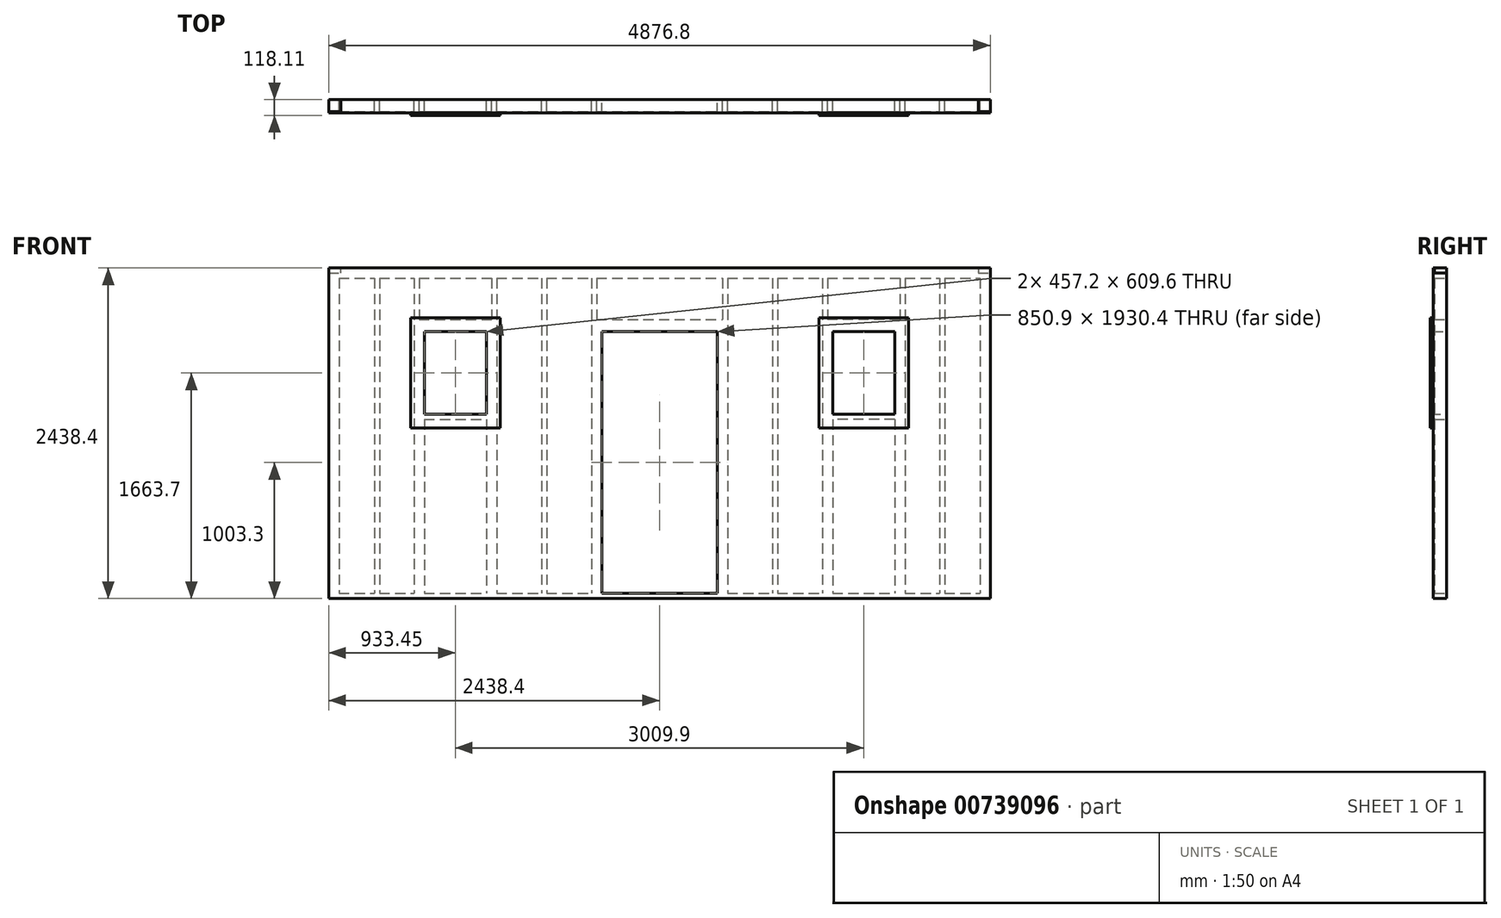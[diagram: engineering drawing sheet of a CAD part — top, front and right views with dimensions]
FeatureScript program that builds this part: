
annotation { "Feature Type Name" : "Feature", "Feature Type Description" : "" }
export const myFeature = defineFeature(function(context is Context, id is Id, definition is map)
    precondition{}
    {
        {
            var Q0;
            Q0=qCreatedBy(makeId("Front.planeOp"),FACE);
            var sketch = newSketch(context, id + "F0", { "sketchPlane" : qUnion([Q0]), "disableImprinting" : false});
            skLineSegment(sketch, "E0.bottom", {"start": v(0, 0) * mm, "end": v(4876.8, 0) * mm});
            skLineSegment(sketch, "E0.top", {"start": v(0, 2400.3) * mm, "end": v(4876.8, 2400.3) * mm});
            skLineSegment(sketch, "E0.left", {"start": v(0, 0) * mm, "end": v(0, 2400.3) * mm});
            skLineSegment(sketch, "E0.right", {"start": v(4876.8, 0) * mm, "end": v(4876.8, 2400.3) * mm});
            skLineSegment(sketch, "E1.0", {"start": v(0, 38.1) * mm, "end": v(4876.8, 38.1) * mm});
            skLineSegment(sketch, "E2.0", {"start": v(0, 2362.2) * mm, "end": v(4876.8, 2362.2) * mm});
            skLineSegment(sketch, "E3", {"start": v(38.1, 2362.2) * mm, "end": v(38.1, 38.1) * mm});
            skLineSegment(sketch, "E4.0", {"start": v(76.2, 2362.2) * mm, "end": v(76.2, 38.1) * mm});
            skLineSegment(sketch, "E5", {"start": v(4838.7, 2362.2) * mm, "end": v(4838.7, 38.1) * mm});
            skLineSegment(sketch, "E6.0", {"start": v(4800.6, 2362.2) * mm, "end": v(4800.6, 38.1) * mm});
            skLineSegment(sketch, "E7", {"start": v(336.55, 2362.2) * mm, "end": v(336.55, 38.1) * mm});
            skLineSegment(sketch, "E8.0", {"start": v(374.65, 2362.2) * mm, "end": v(374.65, 38.1) * mm});
            skLineSegment(sketch, "E9", {"start": v(628.65, 2362.2) * mm, "end": v(628.65, 38.1) * mm});
            skLineSegment(sketch, "E10.0", {"start": v(666.75, 2362.2) * mm, "end": v(666.75, 38.1) * mm});
            skLineSegment(sketch, "E11", {"start": v(1200.15, 2362.2) * mm, "end": v(1200.15, 38.1) * mm});
            skLineSegment(sketch, "E12.0", {"start": v(1238.25, 2362.2) * mm, "end": v(1238.25, 38.1) * mm});
            skLineSegment(sketch, "E13", {"start": v(666.75, 1968.5) * mm, "end": v(1200.15, 1968.5) * mm});
            skLineSegment(sketch, "E14.0", {"start": v(666.75, 2057.4) * mm, "end": v(1200.15, 2057.4) * mm});
            skLineSegment(sketch, "E15", {"start": v(666.75, 1358.9) * mm, "end": v(1200.15, 1358.9) * mm});
            skLineSegment(sketch, "E16.0", {"start": v(666.75, 1320.8) * mm, "end": v(1200.15, 1320.8) * mm});
            skLineSegment(sketch, "E17", {"start": v(704.85, 1968.5) * mm, "end": v(704.85, 1358.9) * mm});
            skLineSegment(sketch, "E18", {"start": v(1162.05, 1968.5) * mm, "end": v(1162.05, 1358.9) * mm});
            skLineSegment(sketch, "E19", {"start": v(2438.4, 2362.2) * mm, "end": v(2438.4, -1355.37) * mm, "construction": true});
            skLineSegment(sketch, "E20", {"start": v(88.9, 2400.3) * mm, "end": v(88.9, 2438.4) * mm});
            skLineSegment(sketch, "E21", {"start": v(88.9, 2438.4) * mm, "end": v(4787.9, 2438.4) * mm});
            skLineSegment(sketch, "E22", {"start": v(4787.9, 2438.4) * mm, "end": v(4787.9, 2400.3) * mm});
            skLineSegment(sketch, "E23", {"start": v(1568.45, 2362.2) * mm, "end": v(1568.45, 38.1) * mm});
            skLineSegment(sketch, "E24", {"start": v(1606.55, 2362.2) * mm, "end": v(1606.55, 38.1) * mm});
            skLineSegment(sketch, "E25.MirrorCS", {"start": v(4210.05, 1320.8) * mm, "end": v(3676.65, 1320.8) * mm});
            skLineSegment(sketch, "E26.MirrorCS", {"start": v(4540.25, 2362.2) * mm, "end": v(4540.25, 38.1) * mm});
            skLineSegment(sketch, "E27.MirrorCS", {"start": v(4502.15, 2362.2) * mm, "end": v(4502.15, 38.1) * mm});
            skLineSegment(sketch, "E28.MirrorCS", {"start": v(4248.15, 2362.2) * mm, "end": v(4248.15, 38.1) * mm});
            skLineSegment(sketch, "E29.MirrorCS", {"start": v(3270.25, 2362.2) * mm, "end": v(3270.25, 38.1) * mm});
            skLineSegment(sketch, "E30.MirrorCS", {"start": v(4171.95, 1968.5) * mm, "end": v(4171.95, 1358.9) * mm});
            skLineSegment(sketch, "E31.MirrorCS", {"start": v(4210.05, 1968.5) * mm, "end": v(3676.65, 1968.5) * mm});
            skLineSegment(sketch, "E32.MirrorCS", {"start": v(3714.75, 1968.5) * mm, "end": v(3714.75, 1358.9) * mm});
            skLineSegment(sketch, "E33.MirrorCS", {"start": v(4210.05, 1358.9) * mm, "end": v(3676.65, 1358.9) * mm});
            skLineSegment(sketch, "E34.MirrorCS", {"start": v(3308.35, 2362.2) * mm, "end": v(3308.35, 38.1) * mm});
            skLineSegment(sketch, "E35.MirrorCS", {"start": v(4210.05, 2057.4) * mm, "end": v(3676.65, 2057.4) * mm});
            skLineSegment(sketch, "E36.MirrorCS", {"start": v(4210.05, 2362.2) * mm, "end": v(4210.05, 38.1) * mm});
            skLineSegment(sketch, "E37.MirrorCS", {"start": v(3638.55, 2362.2) * mm, "end": v(3638.55, 38.1) * mm});
            skLineSegment(sketch, "E38.MirrorCS", {"start": v(3676.65, 2362.2) * mm, "end": v(3676.65, 38.1) * mm});
            skLineSegment(sketch, "E39", {"start": v(1219.2, 2813.17) * mm, "end": v(1219.2, -1320.33) * mm, "construction": true});
            skLineSegment(sketch, "E40", {"start": v(1936.75, 2362.2) * mm, "end": v(1936.75, 38.1) * mm});
            skLineSegment(sketch, "E41", {"start": v(1974.85, 2362.2) * mm, "end": v(1974.85, 38.1) * mm});
            skLineSegment(sketch, "E42.MirrorCS", {"start": v(2901.95, 2362.2) * mm, "end": v(2901.95, 38.1) * mm});
            skLineSegment(sketch, "E43.MirrorCS", {"start": v(2940.05, 2362.2) * mm, "end": v(2940.05, 38.1) * mm});
            skLineSegment(sketch, "E44", {"start": v(704.85, 1320.8) * mm, "end": v(704.85, 38.1) * mm});
            skLineSegment(sketch, "E45", {"start": v(1162.05, 1320.8) * mm, "end": v(1162.05, 38.1) * mm});
            skLineSegment(sketch, "E46", {"start": v(895.35, 2362.2) * mm, "end": v(895.35, 2057.4) * mm});
            skLineSegment(sketch, "E47", {"start": v(933.45, 2362.2) * mm, "end": v(933.45, 2057.4) * mm});
            skLineSegment(sketch, "E48", {"start": v(1974.85, 2057.4) * mm, "end": v(2901.95, 2057.4) * mm});
            skLineSegment(sketch, "E49", {"start": v(1974.85, 1968.5) * mm, "end": v(2901.95, 1968.5) * mm});
            skLineSegment(sketch, "E50", {"start": v(2012.95, 1968.5) * mm, "end": v(2012.95, 38.1) * mm});
            skLineSegment(sketch, "E51.MirrorCS", {"start": v(2863.85, 1968.5) * mm, "end": v(2863.85, 38.1) * mm});
            skLineSegment(sketch, "E52", {"start": v(3714.75, 1320.8) * mm, "end": v(3714.75, 38.1) * mm});
            skLineSegment(sketch, "E53", {"start": v(4171.95, 1320.8) * mm, "end": v(4171.95, 38.1) * mm});
            skSolve(sketch);
        }
        {
            var Q0;
            {var subQ5=sQuery(id+"F0.wireOp",EDGE,"E3");Q0=makeQuery(id+"F0.imprint","IMPRINT",FACE,{"disambiguationData":[TD([[makeQuery(id+"F0.imprint","IMPRINT",EDGE,{"derivedFrom":subQ5}),-1.0]])]});}
            var Q1;
            {var subQ0=sQuery(id+"F0.wireOp",EDGE,"E3");Q1=makeQuery(id+"F0.imprint","IMPRINT",FACE,{"disambiguationData":[TD([[makeQuery(id+"F0.imprint","IMPRINT",EDGE,{"derivedFrom":subQ0}),1.0]])]});}
            var Q2;
            {var subQ15=sQuery(id+"F0.wireOp",EDGE,"E0.bottom");Q2=makeQuery(id+"F0.imprint","IMPRINT",FACE,{"disambiguationData":[TD([[makeQuery(id+"F0.imprint","IMPRINT",EDGE,{"derivedFrom":subQ15}),1.0]])]});}
            var Q3;
            {var subQ0=sQuery(id+"F0.wireOp",EDGE,"E7");Q3=makeQuery(id+"F0.imprint","IMPRINT",FACE,{"disambiguationData":[TD([[makeQuery(id+"F0.imprint","IMPRINT",EDGE,{"derivedFrom":subQ0}),1.0]])]});}
            var Q4;
            {var subQ4=sQuery(id+"F0.wireOp",EDGE,"E9");Q4=makeQuery(id+"F0.imprint","IMPRINT",FACE,{"disambiguationData":[TD([[makeQuery(id+"F0.imprint","IMPRINT",EDGE,{"derivedFrom":subQ4}),1.0]])]});}
            var Q5;
            {var subQ5=sQuery(id+"F0.wireOp",EDGE,"E12.0");Q5=makeQuery(id+"F0.imprint","IMPRINT",FACE,{"disambiguationData":[TD([[makeQuery(id+"F0.imprint","IMPRINT",EDGE,{"derivedFrom":subQ5}),-1.0]])]});}
            var Q6;
            {var subQ5=sQuery(id+"F0.wireOp",EDGE,"E14.0");Q6=makeQuery(id+"F0.imprint","IMPRINT",FACE,{"disambiguationData":[TD([[makeQuery(id+"F0.imprint","IMPRINT",EDGE,{"derivedFrom":subQ5}),-1.0]])]});}
            var Q7;
            {var subQ5=sQuery(id+"F0.wireOp",EDGE,"E17");Q7=makeQuery(id+"F0.imprint","IMPRINT",FACE,{"disambiguationData":[TD([[makeQuery(id+"F0.imprint","IMPRINT",EDGE,{"derivedFrom":subQ5}),-1.0]])]});}
            var Q8;
            {var subQ5=sQuery(id+"F0.wireOp",EDGE,"E18");Q8=makeQuery(id+"F0.imprint","IMPRINT",FACE,{"disambiguationData":[TD([[makeQuery(id+"F0.imprint","IMPRINT",EDGE,{"derivedFrom":subQ5}),1.0]])]});}
            var Q9;
            {var subQ7=sQuery(id+"F0.wireOp",EDGE,"E16.0");Q9=makeQuery(id+"F0.imprint","IMPRINT",FACE,{"disambiguationData":[TD([[makeQuery(id+"F0.imprint","IMPRINT",EDGE,{"derivedFrom":subQ7}),1.0]])]});}
            var Q10;
            {var subQ14=sQuery(id+"F0.wireOp",EDGE,"E0.top");var subQ22=sQuery(id+"F0.wireOp",EDGE,"E0.left");var subQ23=makeQuery(id+"F0.imprint","INTERSECT",VERTEX,{"derivedFrom":[subQ14,subQ22]});Q10=makeQuery(id+"F0.imprint","IMPRINT",FACE,{"disambiguationData":[TD([[makeQuery(id+"F0.imprint","IMPRINT",EDGE,{"disambiguationData":[TD([[subQ23,-1.0]])],"derivedFrom":subQ14}),-1.0]])]});}
            var Q11;
            {var subQ0=sQuery(id+"F0.wireOp",EDGE,"E20");Q11=makeQuery(id+"F0.imprint","IMPRINT",FACE,{"disambiguationData":[TD([[makeQuery(id+"F0.imprint","IMPRINT",EDGE,{"derivedFrom":subQ0}),-1.0]])]});}
            var Q12;
            {var subQ0=sQuery(id+"F0.wireOp",EDGE,"E23");Q12=makeQuery(id+"F0.imprint","IMPRINT",FACE,{"disambiguationData":[TD([[makeQuery(id+"F0.imprint","IMPRINT",EDGE,{"derivedFrom":subQ0}),1.0]])]});}
            var Q13;
            {var subQ0=sQuery(id+"F0.wireOp",EDGE,"b2736123-43ef-459a-b707-f0dc9522e4d70.MirrorCS");Q13=makeQuery(id+"F0.imprint","IMPRINT",FACE,{"disambiguationData":[TD([[makeQuery(id+"F0.imprint","IMPRINT",EDGE,{"derivedFrom":subQ0}),1.0]])]});}
            var Q14;
            {var subQ5=sQuery(id+"F0.wireOp",EDGE,"e07205b2-3a5f-401d-925a-56d0bd6f891c11.MirrorCS");Q14=makeQuery(id+"F0.imprint","IMPRINT",FACE,{"disambiguationData":[TD([[makeQuery(id+"F0.imprint","IMPRINT",EDGE,{"derivedFrom":subQ5}),1.0]])]});}
            var Q15;
            {var subQ0=sQuery(id+"F0.wireOp",EDGE,"e07205b2-3a5f-401d-925a-56d0bd6f891c0.MirrorCS");Q15=makeQuery(id+"F0.imprint","IMPRINT",FACE,{"disambiguationData":[TD([[makeQuery(id+"F0.imprint","IMPRINT",EDGE,{"derivedFrom":subQ0}),-1.0]])]});}
            var Q16;
            {var subQ3=sQuery(id+"F0.wireOp",EDGE,"e07205b2-3a5f-401d-925a-56d0bd6f891c2.MirrorCS");Q16=makeQuery(id+"F0.imprint","IMPRINT",FACE,{"disambiguationData":[TD([[makeQuery(id+"F0.imprint","IMPRINT",EDGE,{"derivedFrom":subQ3}),1.0]])]});}
            var Q17;
            {var subQ4=sQuery(id+"F0.wireOp",EDGE,"e07205b2-3a5f-401d-925a-56d0bd6f891c4.MirrorCS");Q17=makeQuery(id+"F0.imprint","IMPRINT",FACE,{"disambiguationData":[TD([[makeQuery(id+"F0.imprint","IMPRINT",EDGE,{"derivedFrom":subQ4}),-1.0]])]});}
            var Q18;
            {var subQ3=sQuery(id+"F0.wireOp",EDGE,"e07205b2-3a5f-401d-925a-56d0bd6f891c9.MirrorCS");Q18=makeQuery(id+"F0.imprint","IMPRINT",FACE,{"disambiguationData":[TD([[makeQuery(id+"F0.imprint","IMPRINT",EDGE,{"derivedFrom":subQ3}),1.0]])]});}
            var Q19;
            {var subQ5=sQuery(id+"F0.wireOp",EDGE,"e07205b2-3a5f-401d-925a-56d0bd6f891c7.MirrorCS");Q19=makeQuery(id+"F0.imprint","IMPRINT",FACE,{"disambiguationData":[TD([[makeQuery(id+"F0.imprint","IMPRINT",EDGE,{"derivedFrom":subQ5}),-1.0]])]});}
            var Q20;
            {var subQ0=sQuery(id+"F0.wireOp",EDGE,"e07205b2-3a5f-401d-925a-56d0bd6f891c5.MirrorCS");Q20=makeQuery(id+"F0.imprint","IMPRINT",FACE,{"disambiguationData":[TD([[makeQuery(id+"F0.imprint","IMPRINT",EDGE,{"derivedFrom":subQ0}),1.0]])]});}
            var Q21;
            {var subQ5=sQuery(id+"F0.wireOp",EDGE,"E5");Q21=makeQuery(id+"F0.imprint","IMPRINT",FACE,{"disambiguationData":[TD([[makeQuery(id+"F0.imprint","IMPRINT",EDGE,{"derivedFrom":subQ5}),1.0]])]});}
            var Q22;
            {var subQ0=sQuery(id+"F0.wireOp",EDGE,"E5");Q22=makeQuery(id+"F0.imprint","IMPRINT",FACE,{"disambiguationData":[TD([[makeQuery(id+"F0.imprint","IMPRINT",EDGE,{"derivedFrom":subQ0}),-1.0]])]});}
            var Q23;
            {var subQ0=sQuery(id+"F0.wireOp",EDGE,"Ij9m16tq-twXF-Xwvy-82qe-HxNIa6wjf4lT");Q23=makeQuery(id+"F0.imprint","IMPRINT",FACE,{"disambiguationData":[TD([[makeQuery(id+"F0.imprint","IMPRINT",EDGE,{"derivedFrom":subQ0}),1.0]])]});}
            var Q24;
            {var subQ0=sQuery(id+"F0.wireOp",EDGE,"E29.MirrorCS");Q24=makeQuery(id+"F0.imprint","IMPRINT",FACE,{"disambiguationData":[TD([[makeQuery(id+"F0.imprint","IMPRINT",EDGE,{"derivedFrom":subQ0}),1.0]])]});}
            var Q25;
            {var subQ5=sQuery(id+"F0.wireOp",EDGE,"E25.MirrorCS");Q25=makeQuery(id+"F0.imprint","IMPRINT",FACE,{"disambiguationData":[TD([[makeQuery(id+"F0.imprint","IMPRINT",EDGE,{"derivedFrom":subQ5}),-1.0]])]});}
            var Q26;
            {var subQ3=sQuery(id+"F0.wireOp",EDGE,"E32.MirrorCS");Q26=makeQuery(id+"F0.imprint","IMPRINT",FACE,{"disambiguationData":[TD([[makeQuery(id+"F0.imprint","IMPRINT",EDGE,{"derivedFrom":subQ3}),-1.0]])]});}
            var Q27;
            {var subQ4=sQuery(id+"F0.wireOp",EDGE,"E37.MirrorCS");Q27=makeQuery(id+"F0.imprint","IMPRINT",FACE,{"disambiguationData":[TD([[makeQuery(id+"F0.imprint","IMPRINT",EDGE,{"derivedFrom":subQ4}),1.0]])]});}
            var Q28;
            {var subQ0=sQuery(id+"F0.wireOp",EDGE,"E30.MirrorCS");Q28=makeQuery(id+"F0.imprint","IMPRINT",FACE,{"disambiguationData":[TD([[makeQuery(id+"F0.imprint","IMPRINT",EDGE,{"derivedFrom":subQ0}),1.0]])]});}
            var Q29;
            {var subQ4=sQuery(id+"F0.wireOp",EDGE,"E28.MirrorCS");Q29=makeQuery(id+"F0.imprint","IMPRINT",FACE,{"disambiguationData":[TD([[makeQuery(id+"F0.imprint","IMPRINT",EDGE,{"derivedFrom":subQ4}),-1.0]])]});}
            var Q30;
            {var subQ0=sQuery(id+"F0.wireOp",EDGE,"E35.MirrorCS");Q30=makeQuery(id+"F0.imprint","IMPRINT",FACE,{"disambiguationData":[TD([[makeQuery(id+"F0.imprint","IMPRINT",EDGE,{"derivedFrom":subQ0}),1.0]])]});}
            var Q31;
            {var subQ0=sQuery(id+"F0.wireOp",EDGE,"E26.MirrorCS");Q31=makeQuery(id+"F0.imprint","IMPRINT",FACE,{"disambiguationData":[TD([[makeQuery(id+"F0.imprint","IMPRINT",EDGE,{"derivedFrom":subQ0}),-1.0]])]});}
            var Q32;
            {var subQ0=sQuery(id+"F0.wireOp",EDGE,"E40");Q32=makeQuery(id+"F0.imprint","IMPRINT",FACE,{"disambiguationData":[TD([[makeQuery(id+"F0.imprint","IMPRINT",EDGE,{"derivedFrom":subQ0}),1.0]])]});}
            var Q33;
            {var subQ0=sQuery(id+"F0.wireOp",EDGE,"E42.MirrorCS");Q33=makeQuery(id+"F0.imprint","IMPRINT",FACE,{"disambiguationData":[TD([[makeQuery(id+"F0.imprint","IMPRINT",EDGE,{"derivedFrom":subQ0}),1.0]])]});}
            var Q34;
            {var subQ3=sQuery(id+"F0.wireOp",EDGE,"E50");Q34=makeQuery(id+"F0.imprint","IMPRINT",FACE,{"disambiguationData":[TD([[makeQuery(id+"F0.imprint","IMPRINT",EDGE,{"derivedFrom":subQ3}),-1.0]])]});}
            var Q35;
            {var subQ0=sQuery(id+"F0.wireOp",EDGE,"E48");Q35=makeQuery(id+"F0.imprint","IMPRINT",FACE,{"disambiguationData":[TD([[makeQuery(id+"F0.imprint","IMPRINT",EDGE,{"derivedFrom":subQ0}),-1.0]])]});}
            var Q36;
            {var subQ3=sQuery(id+"F0.wireOp",EDGE,"E51.MirrorCS");Q36=makeQuery(id+"F0.imprint","IMPRINT",FACE,{"disambiguationData":[TD([[makeQuery(id+"F0.imprint","IMPRINT",EDGE,{"derivedFrom":subQ3}),1.0]])]});}
            var Q37;
            {var subQ3=sQuery(id+"F0.wireOp",EDGE,"E52");Q37=makeQuery(id+"F0.imprint","IMPRINT",FACE,{"disambiguationData":[TD([[makeQuery(id+"F0.imprint","IMPRINT",EDGE,{"derivedFrom":subQ3}),-1.0]])]});}
            var Q38;
            {var subQ3=sQuery(id+"F0.wireOp",EDGE,"E53");Q38=makeQuery(id+"F0.imprint","IMPRINT",FACE,{"disambiguationData":[TD([[makeQuery(id+"F0.imprint","IMPRINT",EDGE,{"derivedFrom":subQ3}),1.0]])]});}
            var Q39;
            {var subQ3=sQuery(id+"F0.wireOp",EDGE,"E44");Q39=makeQuery(id+"F0.imprint","IMPRINT",FACE,{"disambiguationData":[TD([[makeQuery(id+"F0.imprint","IMPRINT",EDGE,{"derivedFrom":subQ3}),-1.0]])]});}
            var Q40;
            {var subQ3=sQuery(id+"F0.wireOp",EDGE,"E45");Q40=makeQuery(id+"F0.imprint","IMPRINT",FACE,{"disambiguationData":[TD([[makeQuery(id+"F0.imprint","IMPRINT",EDGE,{"derivedFrom":subQ3}),1.0]])]});}
            extrude(context, id + "F1", {"entities" : qUnion([Q0, Q1, Q2, Q3, Q4, Q5, Q6, Q7, Q8, Q9, Q10, Q11, Q12, Q13, Q14, Q15, Q16, Q17, Q18, Q19, Q20, Q21, Q22, Q23, Q24, Q25, Q26, Q27, Q28, Q29, Q30, Q31, Q32, Q33, Q34, Q35, Q36, Q37, Q38, Q39, Q40]), "depth" : 88.9 * mm, "offsetDistance" : 25.4 * mm});
        }
        {
            var Q0;
            Q0=makeQuery(id+"F1.opExtrude","CAP_FACE",FACE,{"disambiguationData":[OSD([sQuery(id+"F0.wireOp",EDGE,"E0.bottom"),sQuery(id+"F0.wireOp",EDGE,"E0.top"),sQuery(id+"F0.wireOp",EDGE,"E0.left"),sQuery(id+"F0.wireOp",EDGE,"E0.right"),sQuery(id+"F0.wireOp",EDGE,"E1.0"),sQuery(id+"F0.wireOp",EDGE,"E2.0"),sQuery(id+"F0.wireOp",EDGE,"E4.0"),sQuery(id+"F0.wireOp",EDGE,"E6.0"),sQuery(id+"F0.wireOp",EDGE,"E7"),sQuery(id+"F0.wireOp",EDGE,"E8.0"),sQuery(id+"F0.wireOp",EDGE,"E9"),sQuery(id+"F0.wireOp",EDGE,"E10.0"),sQuery(id+"F0.wireOp",EDGE,"E11"),sQuery(id+"F0.wireOp",EDGE,"E12.0"),sQuery(id+"F0.wireOp",EDGE,"E13"),sQuery(id+"F0.wireOp",EDGE,"E14.0"),sQuery(id+"F0.wireOp",EDGE,"E15"),sQuery(id+"F0.wireOp",EDGE,"E16.0"),sQuery(id+"F0.wireOp",EDGE,"E17"),sQuery(id+"F0.wireOp",EDGE,"E18"),sQuery(id+"F0.wireOp",EDGE,"E20"),sQuery(id+"F0.wireOp",EDGE,"E21"),sQuery(id+"F0.wireOp",EDGE,"E22"),sQuery(id+"F0.wireOp",EDGE,"E23"),sQuery(id+"F0.wireOp",EDGE,"E24"),sQuery(id+"F0.wireOp",EDGE,"Ij9m16tq-twXF-Xwvy-82qe-HxNIa6wjf4lT"),sQuery(id+"F0.wireOp",EDGE,"1c3eaa05-d776-4829-aba2-bb672608830b0.MirrorCS"),sQuery(id+"F0.wireOp",EDGE,"E25.MirrorCS"),sQuery(id+"F0.wireOp",EDGE,"E26.MirrorCS"),sQuery(id+"F0.wireOp",EDGE,"E27.MirrorCS"),sQuery(id+"F0.wireOp",EDGE,"E28.MirrorCS"),sQuery(id+"F0.wireOp",EDGE,"E29.MirrorCS"),sQuery(id+"F0.wireOp",EDGE,"E30.MirrorCS"),sQuery(id+"F0.wireOp",EDGE,"E31.MirrorCS"),sQuery(id+"F0.wireOp",EDGE,"E32.MirrorCS"),sQuery(id+"F0.wireOp",EDGE,"E33.MirrorCS"),sQuery(id+"F0.wireOp",EDGE,"E34.MirrorCS"),sQuery(id+"F0.wireOp",EDGE,"E35.MirrorCS"),sQuery(id+"F0.wireOp",EDGE,"E36.MirrorCS"),sQuery(id+"F0.wireOp",EDGE,"E37.MirrorCS"),sQuery(id+"F0.wireOp",EDGE,"E38.MirrorCS"),sQuery(id+"F0.wireOp",EDGE,"E40"),sQuery(id+"F0.wireOp",EDGE,"E41"),sQuery(id+"F0.wireOp",EDGE,"E42.MirrorCS"),sQuery(id+"F0.wireOp",EDGE,"E43.MirrorCS")])],"isStart":false});
            var sketch = newSketch(context, id + "F2", { "sketchPlane" : qUnion([Q0])});
            skLineSegment(sketch, "E54.0", {"start": v(0, 0) * mm, "end": v(0, 2400.3) * mm});
            skLineSegment(sketch, "E55.0", {"start": v(88.9, 2438.4) * mm, "end": v(4787.9, 2438.4) * mm});
            skLineSegment(sketch, "E56.2", {"start": v(4876.8, 0) * mm, "end": v(4876.8, 2400.3) * mm});
            skLineSegment(sketch, "E56.3", {"start": v(0, 0) * mm, "end": v(4876.8, 0) * mm});
            skLineSegment(sketch, "E57.0", {"start": v(704.85, 1968.5) * mm, "end": v(704.85, 1358.9) * mm});
            skLineSegment(sketch, "E57.1", {"start": v(704.85, 1968.5) * mm, "end": v(1162.05, 1968.5) * mm});
            skLineSegment(sketch, "E57.2", {"start": v(1162.05, 1968.5) * mm, "end": v(1162.05, 1358.9) * mm});
            skLineSegment(sketch, "E57.3", {"start": v(704.85, 1358.9) * mm, "end": v(1162.05, 1358.9) * mm});
            skLineSegment(sketch, "E58.0", {"start": v(4171.95, 1968.5) * mm, "end": v(3714.75, 1968.5) * mm});
            skLineSegment(sketch, "E58.1", {"start": v(4171.95, 1968.5) * mm, "end": v(4171.95, 1358.9) * mm});
            skLineSegment(sketch, "E58.2", {"start": v(4171.95, 1358.9) * mm, "end": v(3714.75, 1358.9) * mm});
            skLineSegment(sketch, "E58.3", {"start": v(3714.75, 1968.5) * mm, "end": v(3714.75, 1358.9) * mm});
            skLineSegment(sketch, "E59", {"start": v(4787.9, 2438.4) * mm, "end": v(4876.8, 2438.4) * mm});
            skLineSegment(sketch, "E60", {"start": v(4876.8, 2438.4) * mm, "end": v(4876.8, 2400.3) * mm});
            skLineSegment(sketch, "E61", {"start": v(0, 2400.3) * mm, "end": v(0, 2438.4) * mm});
            skLineSegment(sketch, "E62", {"start": v(0, 2438.4) * mm, "end": v(88.9, 2438.4) * mm});
            skLineSegment(sketch, "E63.0", {"start": v(2012.95, 1968.5) * mm, "end": v(2012.95, 38.1) * mm});
            skLineSegment(sketch, "E63.1", {"start": v(2863.85, 1968.5) * mm, "end": v(2863.85, 38.1) * mm});
            skLineSegment(sketch, "E63.2", {"start": v(2012.95, 38.1) * mm, "end": v(2863.85, 38.1) * mm});
            skLineSegment(sketch, "E63.3", {"start": v(2012.95, 1968.5) * mm, "end": v(2863.85, 1968.5) * mm});
            skSolve(sketch);
        }
        {
            var Q0;
            Q0 = qSketchRegion(id + "F2", true);
            extrude(context, id + "F3", {"entities" : qUnion([Q0]), "operationType" : NewBodyOperationType.ADD, "depth" : 10.16 * mm, "offsetDistance" : 25.4 * mm});
        }
        {
            var Q0;
            Q0=makeQuery(id+"F3.opExtrude","CAP_FACE",FACE,{"disambiguationData":[OSD([sQuery(id+"F2.wireOp",EDGE,"E54.0"),sQuery(id+"F2.wireOp",EDGE,"E55.0"),sQuery(id+"F2.wireOp",EDGE,"E56.2"),sQuery(id+"F2.wireOp",EDGE,"E56.3"),sQuery(id+"F2.wireOp",EDGE,"E57.0"),sQuery(id+"F2.wireOp",EDGE,"E57.1"),sQuery(id+"F2.wireOp",EDGE,"E57.2"),sQuery(id+"F2.wireOp",EDGE,"E57.3"),sQuery(id+"F2.wireOp",EDGE,"E58.0"),sQuery(id+"F2.wireOp",EDGE,"E58.1"),sQuery(id+"F2.wireOp",EDGE,"E58.2"),sQuery(id+"F2.wireOp",EDGE,"E58.3"),sQuery(id+"F2.wireOp",EDGE,"E59"),sQuery(id+"F2.wireOp",EDGE,"E60"),sQuery(id+"F2.wireOp",EDGE,"E61"),sQuery(id+"F2.wireOp",EDGE,"E62")])],"isStart":false});
            var sketch = newSketch(context, id + "F4", { "sketchPlane" : qUnion([Q0])});
            skLineSegment(sketch, "E64.0", {"start": v(704.85, 1968.5) * mm, "end": v(704.85, 1358.9) * mm});
            skLineSegment(sketch, "E64.1", {"start": v(704.85, 1968.5) * mm, "end": v(1162.05, 1968.5) * mm});
            skLineSegment(sketch, "E64.2", {"start": v(1162.05, 1968.5) * mm, "end": v(1162.05, 1358.9) * mm});
            skLineSegment(sketch, "E64.3", {"start": v(704.85, 1358.9) * mm, "end": v(1162.05, 1358.9) * mm});
            skPoint(sketch, "E64.4", {"position": v(704.85, 1663.7) * mm});
            skLineSegment(sketch, "E65.0", {"start": v(603.25, 2070.1) * mm, "end": v(603.25, 1257.3) * mm});
            skLineSegment(sketch, "E65.1", {"start": v(603.25, 2070.1) * mm, "end": v(1263.65, 2070.1) * mm});
            skLineSegment(sketch, "E65.2", {"start": v(1263.65, 2070.1) * mm, "end": v(1263.65, 1257.3) * mm});
            skLineSegment(sketch, "E65.3", {"start": v(603.25, 1257.3) * mm, "end": v(1263.65, 1257.3) * mm});
            skLineSegment(sketch, "E66.0", {"start": v(3714.75, 1968.5) * mm, "end": v(3714.75, 1358.9) * mm});
            skLineSegment(sketch, "E66.1", {"start": v(4171.95, 1358.9) * mm, "end": v(3714.75, 1358.9) * mm});
            skLineSegment(sketch, "E66.2", {"start": v(4171.95, 1968.5) * mm, "end": v(4171.95, 1358.9) * mm});
            skLineSegment(sketch, "E66.3", {"start": v(4171.95, 1968.5) * mm, "end": v(3714.75, 1968.5) * mm});
            skLineSegment(sketch, "E67.0", {"start": v(3613.15, 2070.1) * mm, "end": v(3613.15, 1257.3) * mm});
            skLineSegment(sketch, "E67.1", {"start": v(4273.55, 2070.1) * mm, "end": v(3613.15, 2070.1) * mm});
            skLineSegment(sketch, "E67.2", {"start": v(4273.55, 2070.1) * mm, "end": v(4273.55, 1257.3) * mm});
            skLineSegment(sketch, "E67.3", {"start": v(4273.55, 1257.3) * mm, "end": v(3613.15, 1257.3) * mm});
            skSolve(sketch);
        }
        {
            var Q0;
            Q0=makeQuery(id+"F4.imprint","IMPRINT",FACE,{"disambiguationData":[TD([[makeQuery(id+"F4.imprint","IMPRINT",EDGE,{"derivedFrom":sQuery(id+"F4.wireOp",EDGE,"E64.0")}),-1.0]])]});
            var Q1;
            Q1=makeQuery(id+"F4.imprint","IMPRINT",FACE,{"disambiguationData":[TD([[makeQuery(id+"F4.imprint","IMPRINT",EDGE,{"derivedFrom":sQuery(id+"F4.wireOp",EDGE,"E66.0")}),-1.0]])]});
            extrude(context, id + "F5", {"entities" : qUnion([Q0, Q1]), "operationType" : NewBodyOperationType.ADD, "depth" : 19.05 * mm, "offsetDistance" : 25.4 * mm});
        }
    });
